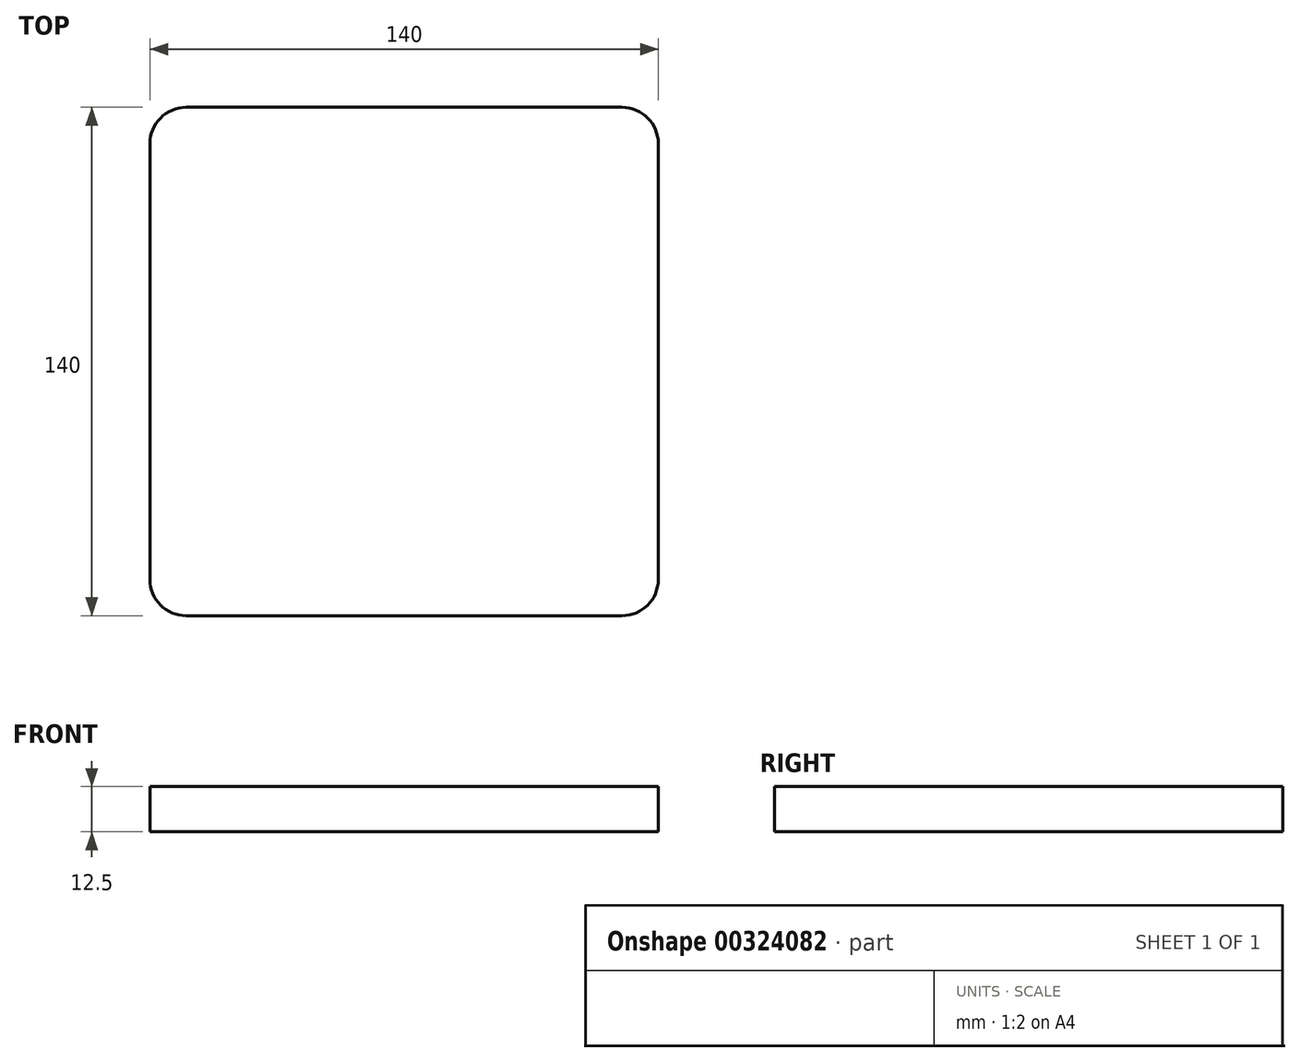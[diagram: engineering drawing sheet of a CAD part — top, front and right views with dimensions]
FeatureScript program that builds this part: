
annotation { "Feature Type Name" : "Feature", "Feature Type Description" : "" }
export const myFeature = defineFeature(function(context is Context, id is Id, definition is map)
    precondition{}
    {
        {
            var Q0;
            Q0=qCreatedBy(makeId("Top.planeOp"),FACE);
            var sketch = newSketch(context, id + "F0", { "sketchPlane" : qUnion([Q0])});
            skLineSegment(sketch, "E0.bottom", {"start": v(70, 70) * mm, "end": v(-70, 70) * mm});
            skLineSegment(sketch, "E0.top", {"start": v(70, -70) * mm, "end": v(-70, -70) * mm});
            skLineSegment(sketch, "E0.left", {"start": v(70, 70) * mm, "end": v(70, -70) * mm});
            skLineSegment(sketch, "E0.right", {"start": v(-70, 70) * mm, "end": v(-70, -70) * mm});
            skPoint(sketch, "E0.middle", {"position": v(0, 0) * mm});
            skLineSegment(sketch, "E1.bottom", {"start": v(-20, 65) * mm, "end": v(20, 65) * mm});
            skLineSegment(sketch, "E1.top", {"start": v(-20, -65) * mm, "end": v(20, -65) * mm});
            skLineSegment(sketch, "E1.left", {"start": v(-20, 65) * mm, "end": v(-20, -65) * mm});
            skLineSegment(sketch, "E1.right", {"start": v(20, 65) * mm, "end": v(20, -65) * mm});
            skSolve(sketch);
        }
        {
            var Q0;
            Q0=makeQuery(id+"F0.imprint","IMPRINT",FACE,{"disambiguationData":[TD([[makeQuery(id+"F0.imprint","IMPRINT",EDGE,{"derivedFrom":sQuery(id+"F0.wireOp",EDGE,"E0.bottom")}),1.0]])]});
            var Q1;
            Q1=makeQuery(id+"F0.imprint","IMPRINT",FACE,{"disambiguationData":[TD([[makeQuery(id+"F0.imprint","IMPRINT",EDGE,{"derivedFrom":sQuery(id+"F0.wireOp",EDGE,"E1.bottom")}),-1.0]])]});
            extrude(context, id + "F1", {"entities" : qUnion([Q0, Q1]), "depth" : 12.5 * mm});
        }
        {
            var Q0;
            Q0=makeQuery(id+"F1.opExtrude","SWEPT_EDGE",EDGE,{"disambiguationData":[OSD([sQuery(id+"F0.wireOp",EDGE,"E0.top"),sQuery(id+"F0.wireOp",EDGE,"E0.left")])]});
            var Q1;
            Q1=makeQuery(id+"F1.opExtrude","SWEPT_EDGE",EDGE,{"disambiguationData":[OSD([sQuery(id+"F0.wireOp",EDGE,"E0.bottom"),sQuery(id+"F0.wireOp",EDGE,"E0.left")])]});
            var Q2;
            Q2=makeQuery(id+"F1.opExtrude","SWEPT_EDGE",EDGE,{"disambiguationData":[OSD([sQuery(id+"F0.wireOp",EDGE,"E0.bottom"),sQuery(id+"F0.wireOp",EDGE,"E0.right")])]});
            var Q3;
            Q3=makeQuery(id+"F1.opExtrude","SWEPT_EDGE",EDGE,{"disambiguationData":[OSD([sQuery(id+"F0.wireOp",EDGE,"E0.top"),sQuery(id+"F0.wireOp",EDGE,"E0.right")])]});
            fillet(context, id + "F2", {"entities" : qUnion([Q0, Q1, Q2, Q3]), "radius" : 10 * mm, "tangentPropagation" : true, "allowEdgeOverflow" : false});
        }
    });
